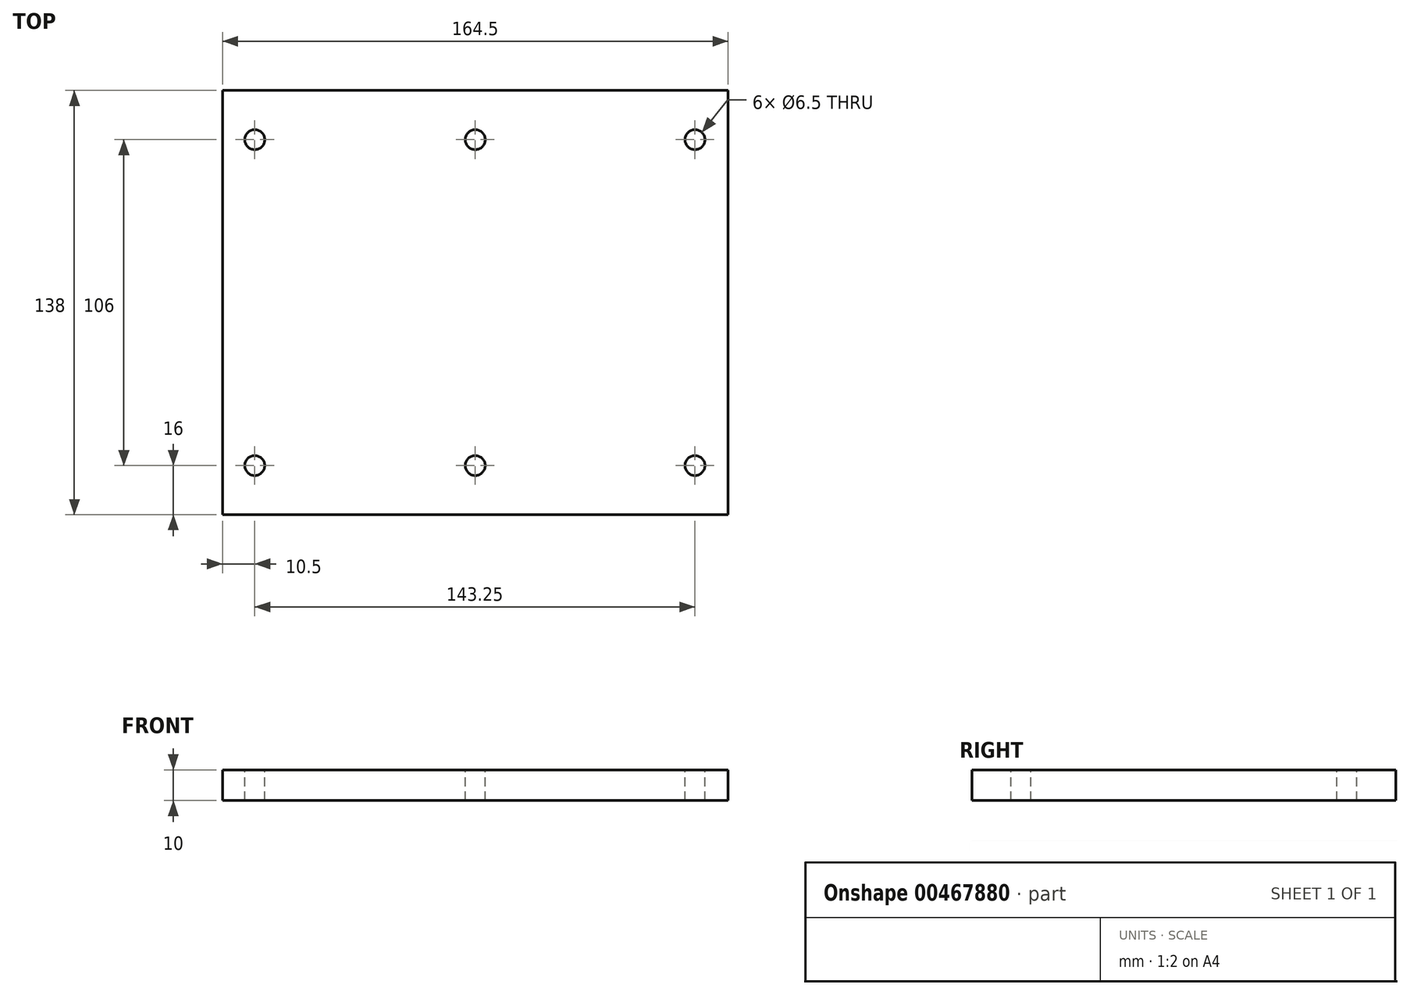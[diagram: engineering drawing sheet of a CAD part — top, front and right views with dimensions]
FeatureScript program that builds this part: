
annotation { "Feature Type Name" : "Feature", "Feature Type Description" : "" }
export const myFeature = defineFeature(function(context is Context, id is Id, definition is map)
    precondition{}
    {
        {
            var Q0;
            Q0=qCreatedBy(makeId("Top.planeOp"),FACE);
            var sketch = newSketch(context, id + "F0", { "sketchPlane" : qUnion([Q0])});
            skLineSegment(sketch, "E0.bottom", {"start": v(0, 0) * mm, "end": v(164.5, 0) * mm});
            skLineSegment(sketch, "E0.top", {"start": v(0, -138) * mm, "end": v(164.5, -138) * mm});
            skLineSegment(sketch, "E0.left", {"start": v(0, 0) * mm, "end": v(0, -138) * mm});
            skLineSegment(sketch, "E0.right", {"start": v(164.5, 0) * mm, "end": v(164.5, -138) * mm});
            skSolve(sketch);
        }
        {
            var Q0;
            Q0=qSketchRegion(id+"F0",true);
            extrude(context, id + "F1", {"entities" : qUnion([Q0]), "depth" : 10 * mm, "offsetDistance" : 25 * mm});
        }
        {
            var Q0;
            Q0=makeQuery(id+"F1.opExtrude","CAP_FACE",FACE,{"disambiguationData":[OSD([sQuery(id+"F0.wireOp",EDGE,"E0.bottom"),sQuery(id+"F0.wireOp",EDGE,"E0.top"),sQuery(id+"F0.wireOp",EDGE,"E0.left"),sQuery(id+"F0.wireOp",EDGE,"E0.right")])],"isStart":false});
            var sketch = newSketch(context, id + "F2", { "sketchPlane" : qUnion([Q0])});
            skCircle(sketch, "E1", {"center": v(153.75, -122) * mm, "radius": 3.25 * mm});
            skCircle(sketch, "E2", {"center": v(153.75, -16) * mm, "radius": 3.25 * mm});
            skCircle(sketch, "E3", {"center": v(82.25, -16) * mm, "radius": 3.25 * mm});
            skCircle(sketch, "E4", {"center": v(10.5, -16) * mm, "radius": 3.25 * mm});
            skCircle(sketch, "E5", {"center": v(82.25, -122) * mm, "radius": 3.25 * mm});
            skCircle(sketch, "E6", {"center": v(10.5, -122) * mm, "radius": 3.25 * mm});
            skSolve(sketch);
        }
        {
            var Q0;
            Q0=qSketchRegion(id+"F2",true);
            extrude(context, id + "F3", {"entities" : qUnion([Q0]), "operationType" : NewBodyOperationType.REMOVE, "oppositeDirection" : true, "depth" : 25 * mm, "offsetDistance" : 25 * mm});
        }
    });
